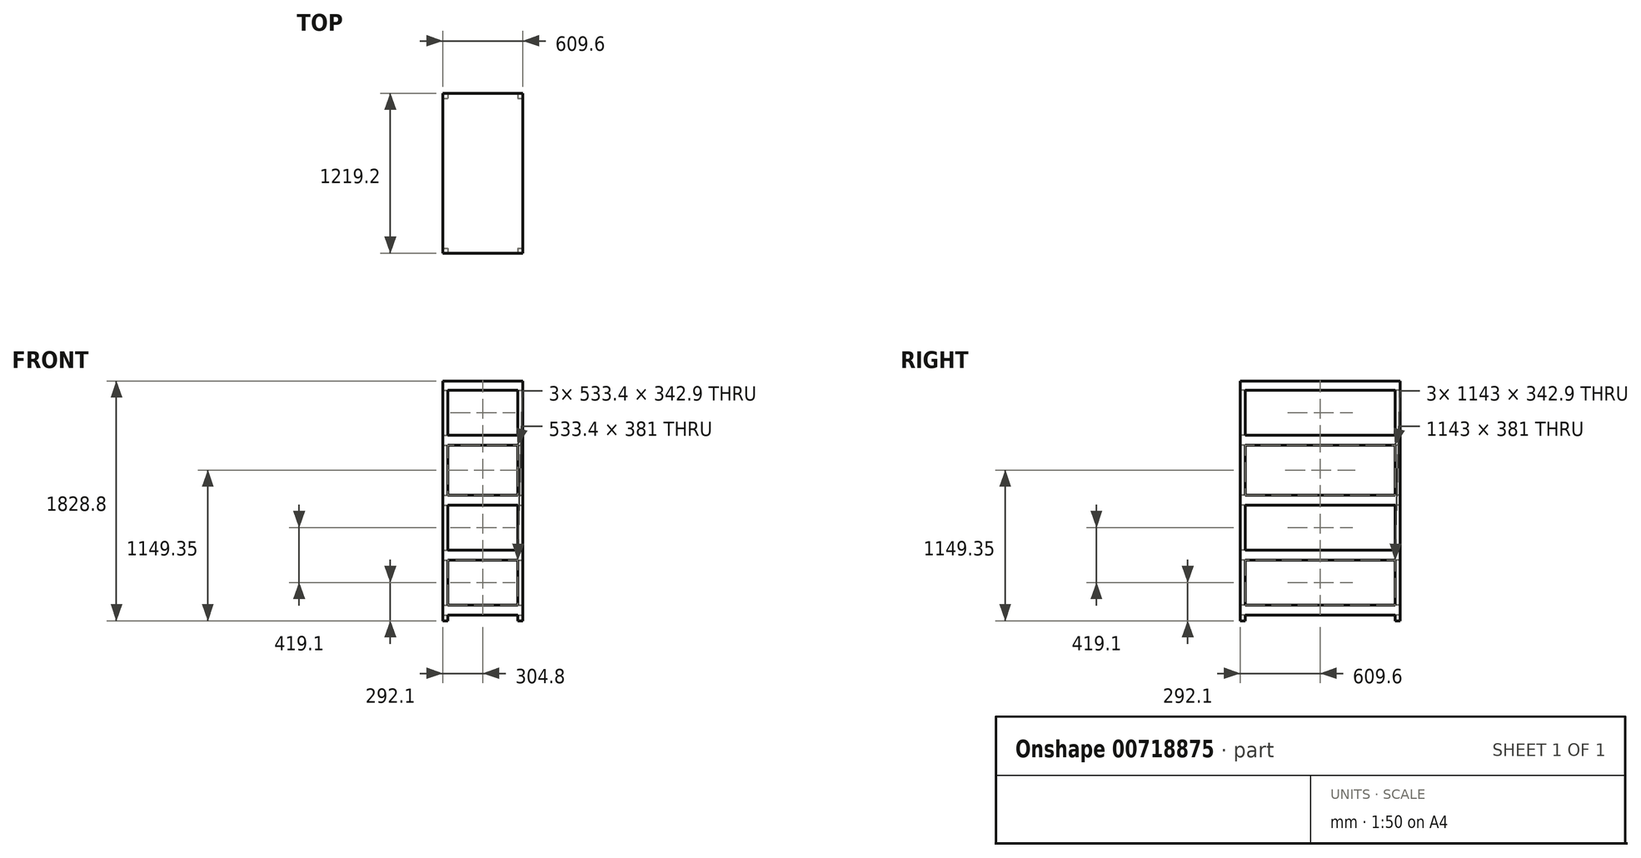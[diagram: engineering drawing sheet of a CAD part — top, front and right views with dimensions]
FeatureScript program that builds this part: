
annotation { "Feature Type Name" : "Feature", "Feature Type Description" : "" }
export const myFeature = defineFeature(function(context is Context, id is Id, definition is map)
    precondition{}
    {
        {
            var Q0;
            Q0=qCreatedBy(makeId("Top.planeOp"),FACE);
            var sketch = newSketch(context, id + "F0", { "sketchPlane" : qUnion([Q0])});
            skLineSegment(sketch, "E0.bottom", {"start": v(-304.8, 609.6) * mm, "end": v(304.8, 609.6) * mm});
            skLineSegment(sketch, "E0.top", {"start": v(-304.8, -609.6) * mm, "end": v(304.8, -609.6) * mm});
            skLineSegment(sketch, "E0.left", {"start": v(-304.8, 609.6) * mm, "end": v(-304.8, -609.6) * mm});
            skLineSegment(sketch, "E0.right", {"start": v(304.8, 609.6) * mm, "end": v(304.8, -609.6) * mm});
            skPoint(sketch, "E0.middle", {"position": v(0, 0) * mm});
            skSolve(sketch);
        }
        {
            var Q0;
            Q0 = qSketchRegion(id + "F0", true);
            extrude(context, id + "F1", {"entities" : qUnion([Q0]), "depth" : 1828.8 * mm, "offsetDistance" : 25.4 * mm});
        }
        {
            var Q0;
            Q0=makeQuery(id+"F1.opExtrude","SWEPT_FACE",FACE,{"disambiguationData":[OSD([sQuery(id+"F0.wireOp",EDGE,"E0.right")])]});
            var sketch = newSketch(context, id + "F2", { "sketchPlane" : qUnion([Q0])});
            skLineSegment(sketch, "E1.bottom", {"start": v(-571.5, 0) * mm, "end": v(571.5, 0) * mm});
            skLineSegment(sketch, "E1.top", {"start": v(-571.5, 44.45) * mm, "end": v(571.5, 44.45) * mm});
            skLineSegment(sketch, "E1.left", {"start": v(-571.5, 0) * mm, "end": v(-571.5, 44.45) * mm});
            skLineSegment(sketch, "E1.right", {"start": v(571.5, 0) * mm, "end": v(571.5, 44.45) * mm});
            skLineSegment(sketch, "E2.bottom", {"start": v(-571.5, 463.55) * mm, "end": v(571.5, 463.55) * mm});
            skLineSegment(sketch, "E2.top", {"start": v(-571.5, 120.65) * mm, "end": v(571.5, 120.65) * mm});
            skLineSegment(sketch, "E2.left", {"start": v(-571.5, 463.55) * mm, "end": v(-571.5, 120.65) * mm});
            skLineSegment(sketch, "E2.right", {"start": v(571.5, 463.55) * mm, "end": v(571.5, 120.65) * mm});
            skLineSegment(sketch, "E3.bottom", {"start": v(-571.5, 882.65) * mm, "end": v(571.5, 882.65) * mm});
            skLineSegment(sketch, "E3.top", {"start": v(-571.5, 539.75) * mm, "end": v(571.5, 539.75) * mm});
            skLineSegment(sketch, "E3.left", {"start": v(-571.5, 882.65) * mm, "end": v(-571.5, 539.75) * mm});
            skLineSegment(sketch, "E3.right", {"start": v(571.5, 882.65) * mm, "end": v(571.5, 539.75) * mm});
            skLineSegment(sketch, "E4.bottom", {"start": v(-571.5, 1339.85) * mm, "end": v(571.5, 1339.85) * mm});
            skLineSegment(sketch, "E4.top", {"start": v(-571.5, 958.85) * mm, "end": v(571.5, 958.85) * mm});
            skLineSegment(sketch, "E4.left", {"start": v(-571.5, 1339.85) * mm, "end": v(-571.5, 958.85) * mm});
            skLineSegment(sketch, "E4.right", {"start": v(571.5, 1339.85) * mm, "end": v(571.5, 958.85) * mm});
            skLineSegment(sketch, "E5.bottom", {"start": v(-571.5, 1758.95) * mm, "end": v(571.5, 1758.95) * mm});
            skLineSegment(sketch, "E5.top", {"start": v(-571.5, 1416.05) * mm, "end": v(571.5, 1416.05) * mm});
            skLineSegment(sketch, "E5.left", {"start": v(-571.5, 1758.95) * mm, "end": v(-571.5, 1416.05) * mm});
            skLineSegment(sketch, "E5.right", {"start": v(571.5, 1758.95) * mm, "end": v(571.5, 1416.05) * mm});
            skSolve(sketch);
        }
        {
            var Q0;
            Q0 = qSketchRegion(id + "F2", true);
            extrude(context, id + "F3", {"entities" : qUnion([Q0]), "operationType" : NewBodyOperationType.REMOVE, "oppositeDirection" : true, "depth" : 2656.84 * mm, "offsetDistance" : 25.4 * mm});
        }
        {
            var Q0;
            Q0=makeQuery(id+"F1.opExtrude","SWEPT_FACE",FACE,{"disambiguationData":[OSD([sQuery(id+"F0.wireOp",EDGE,"E0.top")])]});
            var sketch = newSketch(context, id + "F4", { "sketchPlane" : qUnion([Q0])});
            skLineSegment(sketch, "E6.bottom", {"start": v(-266.7, 0) * mm, "end": v(266.7, 0) * mm});
            skLineSegment(sketch, "E6.top", {"start": v(-266.7, 44.45) * mm, "end": v(266.7, 44.45) * mm});
            skLineSegment(sketch, "E6.left", {"start": v(-266.7, 0) * mm, "end": v(-266.7, 44.45) * mm});
            skLineSegment(sketch, "E6.right", {"start": v(266.7, 0) * mm, "end": v(266.7, 44.45) * mm});
            skLineSegment(sketch, "E7.bottom", {"start": v(-266.7, 539.75) * mm, "end": v(266.7, 539.75) * mm});
            skLineSegment(sketch, "E7.top", {"start": v(-266.7, 120.65) * mm, "end": v(266.7, 120.65) * mm});
            skLineSegment(sketch, "E7.right", {"start": v(266.7, 463.55) * mm, "end": v(266.7, 120.65) * mm});
            skLineSegment(sketch, "E8.bottom", {"start": v(-266.7, 958.85) * mm, "end": v(266.7, 958.85) * mm});
            skLineSegment(sketch, "E8.top", {"start": v(-266.7, 882.65) * mm, "end": v(266.7, 882.65) * mm});
            skLineSegment(sketch, "E9.bottom", {"start": v(-266.7, 1416.05) * mm, "end": v(266.7, 1416.05) * mm});
            skLineSegment(sketch, "E9.top", {"start": v(-266.7, 1339.85) * mm, "end": v(266.7, 1339.85) * mm});
            skLineSegment(sketch, "E10.bottom", {"start": v(-266.7, 463.55) * mm, "end": v(266.7, 463.55) * mm});
            skLineSegment(sketch, "E10.top", {"start": v(-266.7, 1758.95) * mm, "end": v(266.7, 1758.95) * mm});
            skLineSegment(sketch, "E10.right", {"start": v(266.7, 882.65) * mm, "end": v(266.7, 539.75) * mm});
            skLineSegment(sketch, "E11.trimOffspring", {"start": v(266.7, 1758.95) * mm, "end": v(266.7, 1416.05) * mm});
            skLineSegment(sketch, "E12.trimOffspring", {"start": v(-266.7, 1758.95) * mm, "end": v(-266.7, 1416.05) * mm});
            skLineSegment(sketch, "E13.trimOffspring", {"start": v(266.7, 1339.85) * mm, "end": v(266.7, 958.85) * mm});
            skLineSegment(sketch, "E14.trimOffspring", {"start": v(-266.7, 1339.85) * mm, "end": v(-266.7, 958.85) * mm});
            skLineSegment(sketch, "E15", {"start": v(-266.7, 882.65) * mm, "end": v(-266.7, 539.75) * mm});
            skLineSegment(sketch, "E16", {"start": v(-266.7, 463.55) * mm, "end": v(-266.7, 120.65) * mm});
            skSolve(sketch);
        }
        {
            var Q0;
            Q0 = qSketchRegion(id + "F4", true);
            extrude(context, id + "F5", {"entities" : qUnion([Q0]), "operationType" : NewBodyOperationType.REMOVE, "oppositeDirection" : true, "depth" : 1470.66 * mm, "offsetDistance" : 25.4 * mm});
        }
    });
